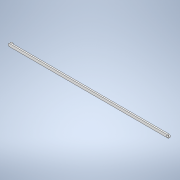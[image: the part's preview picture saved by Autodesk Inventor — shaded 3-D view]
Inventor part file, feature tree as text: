
AUTODESK INVENTOR PART (.ipt)
format: ipt  version: 2021 (Build 250183000, 183)  size: 112,640 bytes
history: native  units: in
note: dims shown in document units (in); Inventor stores cm internally (conversion verified against a paired STEP export)
features: extrude x3, sketch x3, other x1
ambient origin geometry x8: Origin, YZ Plane, XZ Plane, XY Plane, X Axis, Y Axis, Z Axis, Center Point
bodies: Body1 (feature_tree)
feature tree (7):
  other  "Sólido1"
  extrude  "Extrusión1"  Depth=14.3307in
  extrude  "Extrusión2"  Depth=0.125in TaperAngle=0.0deg
  extrude  "Extrusión3"  Depth=0.125in TaperAngle=0.0deg
  sketch  "Boceto1"  dims[d0=0.25in d1=14.3307in]
  sketch  "Boceto2"  dims[d2=0.25in d3=0.125in d4=0.0in]
  sketch  "Boceto3"  dims[d5=0.2106in d6=0.125in d7=0.0in d8=0.2106in d9=0.125in d10=0.0in]
